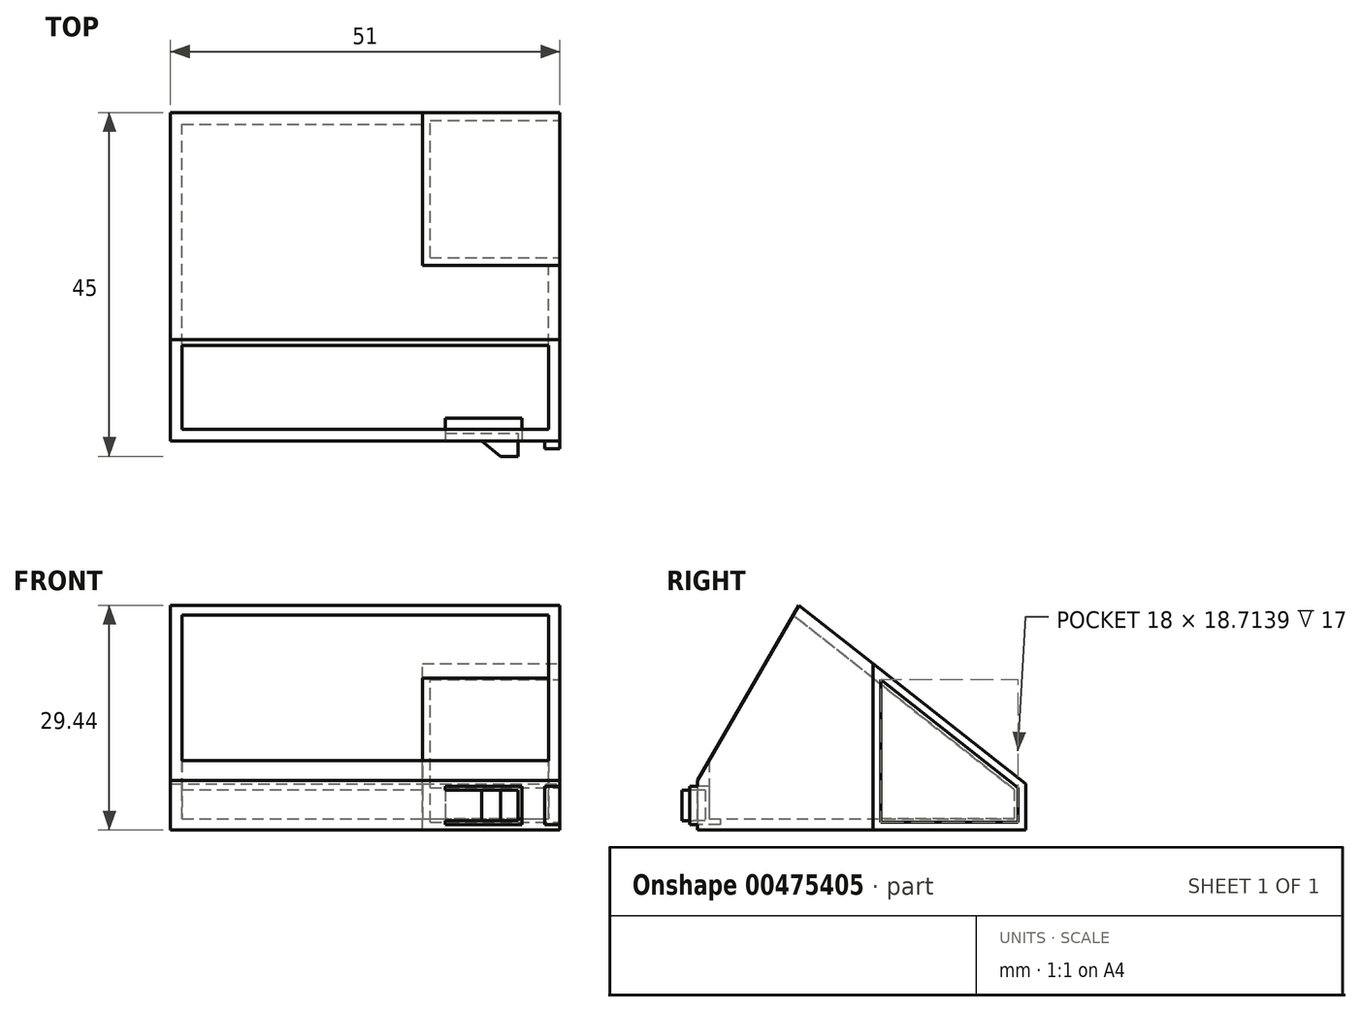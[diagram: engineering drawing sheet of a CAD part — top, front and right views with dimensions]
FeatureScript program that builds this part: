
annotation { "Feature Type Name" : "Feature", "Feature Type Description" : "" }
export const myFeature = defineFeature(function(context is Context, id is Id, definition is map)
    precondition{}
    {
        {
            var Q0;
            Q0=qCreatedBy(makeId("Right.planeOp"),FACE);
            var sketch = newSketch(context, id + "F0", { "sketchPlane" : qUnion([Q0])});
            skLineSegment(sketch, "E0.0", {"start": v(-18.73, 5.62) * mm, "end": v(-18.73, -0.85) * mm});
            skLineSegment(sketch, "E0.1", {"start": v(-5.47, 28.6) * mm, "end": v(-18.73, 5.62) * mm});
            skLineSegment(sketch, "E0.2", {"start": v(-18.73, -0.85) * mm, "end": v(24.27, -0.85) * mm});
            skLineSegment(sketch, "E0.3", {"start": v(24.27, -0.85) * mm, "end": v(24.27, 5.18) * mm});
            skLineSegment(sketch, "E0.4", {"start": v(24.27, 5.18) * mm, "end": v(-5.47, 28.6) * mm});
            skLineSegment(sketch, "E1", {"start": v(4.27, -0.85) * mm, "end": v(4.27, 20.93) * mm});
            skLineSegment(sketch, "E2", {"start": v(-18.73, 5.62) * mm, "end": v(4.27, 5.62) * mm});
            skSolve(sketch);
        }
        {
            var Q0;
            {var subQ0=sQuery(id+"F0.wireOp",EDGE,"E0.0");Q0=makeQuery(id+"F0.imprint","IMPRINT",FACE,{"disambiguationData":[TD([[makeQuery(id+"F0.imprint","IMPRINT",EDGE,{"derivedFrom":subQ0}),1.0]])]});}
            var Q1;
            {var subQ0=sQuery(id+"F0.wireOp",EDGE,"E0.1");Q1=makeQuery(id+"F0.imprint","IMPRINT",FACE,{"disambiguationData":[TD([[makeQuery(id+"F0.imprint","IMPRINT",EDGE,{"derivedFrom":subQ0}),1.0]])]});}
            var Q2;
            {var subQ5=sQuery(id+"F0.wireOp",EDGE,"E0.3");Q2=makeQuery(id+"F0.imprint","IMPRINT",FACE,{"disambiguationData":[TD([[makeQuery(id+"F0.imprint","IMPRINT",EDGE,{"derivedFrom":subQ5}),1.0]])]});}
            extrude(context, id + "F1", {"entities" : qUnion([Q0, Q1, Q2]), "oppositeDirection" : true, "depth" : 51 * mm});
        }
        {
            var Q0;
            Q0=makeQuery(id+"F1.opExtrude","SWEPT_FACE",FACE,{"disambiguationData":[OSD([sQuery(id+"F0.wireOp",EDGE,"E0.1")])]});
            shell(context, id + "F2", {"entities" : qUnion([Q0]), "thickness" : 1.5 * mm});
        }
        {
            var Q0;
            {var subQ5=sQuery(id+"F0.wireOp",EDGE,"E0.3");Q0=makeQuery(id+"F0.imprint","IMPRINT",FACE,{"disambiguationData":[TD([[makeQuery(id+"F0.imprint","IMPRINT",EDGE,{"derivedFrom":subQ5}),1.0]])]});}
            extrude(context, id + "F3", {"entities" : qUnion([Q0]), "operationType" : NewBodyOperationType.REMOVE, "oppositeDirection" : true, "depth" : 18 * mm});
        }
        {
            var Q0;
            {var subQ5=sQuery(id+"F0.wireOp",EDGE,"E0.3");Q0=makeQuery(id+"F0.imprint","IMPRINT",FACE,{"disambiguationData":[TD([[makeQuery(id+"F0.imprint","IMPRINT",EDGE,{"derivedFrom":subQ5}),1.0]])]});}
            extrude(context, id + "F4", {"entities" : qUnion([Q0]), "oppositeDirection" : true, "depth" : 18 * mm});
        }
        {
            var Q0;
            Q0=makeQuery(id+"F4.opExtrude","CAP_FACE",FACE,{"disambiguationData":[OSD([sQuery(id+"F0.wireOp",EDGE,"E0.2"),sQuery(id+"F0.wireOp",EDGE,"E0.3"),sQuery(id+"F0.wireOp",EDGE,"E0.4"),sQuery(id+"F0.wireOp",EDGE,"E1")])],"isStart":true});
            shell(context, id + "F5", {"entities" : qUnion([Q0]), "thickness" : 1 * mm});
        }
        {
            var Q0;
            Q0=makeQuery(id+"F1.opExtrude","SWEPT_FACE",FACE,{"disambiguationData":[OSD([sQuery(id+"F0.wireOp",EDGE,"E0.0")])]});
            var sketch = newSketch(context, id + "F6", { "sketchPlane" : qUnion([Q0])});
            skLineSegment(sketch, "E3.0.0", {"start": v(0, -0.85) * mm, "end": v(0, 5.62) * mm});
            skLineSegment(sketch, "E3.0.1", {"start": v(0, 5.62) * mm, "end": v(-51, 5.62) * mm});
            skLineSegment(sketch, "E3.0.2", {"start": v(-51, 5.62) * mm, "end": v(-51, -0.85) * mm});
            skLineSegment(sketch, "E3.0.3", {"start": v(-51, -0.85) * mm, "end": v(0, -0.85) * mm});
            skLineSegment(sketch, "E4.bottom", {"start": v(-5, 4.89) * mm, "end": v(-15, 4.89) * mm});
            skLineSegment(sketch, "E4.top", {"start": v(-5, -0.11) * mm, "end": v(-15, -0.11) * mm});
            skLineSegment(sketch, "E4.left", {"start": v(-5, 4.89) * mm, "end": v(-5, -0.11) * mm});
            skLineSegment(sketch, "E4.right", {"start": v(-15, 4.89) * mm, "end": v(-15, -0.11) * mm});
            skPoint(sketch, "E4.middle", {"position": v(-10, 2.39) * mm});
            skPoint(sketch, "E4.middle.positionSnap0", {"position": v(0, 2.39) * mm});
            skPoint(sketch, "E4.centerSnap0", {"position": v(0, 2.39) * mm});
            skLineSegment(sketch, "E5", {"start": v(0, 2.39) * mm, "end": v(-27.52, 2.39) * mm, "construction": true});
            skLineSegment(sketch, "E6.bottom", {"start": v(-15, 0.39) * mm, "end": v(-5.5, 0.39) * mm});
            skLineSegment(sketch, "E6.top", {"start": v(-15, 4.39) * mm, "end": v(-5.5, 4.39) * mm});
            skLineSegment(sketch, "E6.left", {"start": v(-15, 0.39) * mm, "end": v(-15, 4.39) * mm});
            skLineSegment(sketch, "E6.right", {"start": v(-5.5, 0.39) * mm, "end": v(-5.5, 4.39) * mm});
            skLineSegment(sketch, "E7.bottom", {"start": v(-2, 4.89) * mm, "end": v(0, 4.89) * mm});
            skLineSegment(sketch, "E7.top", {"start": v(-2, -0.11) * mm, "end": v(0, -0.11) * mm});
            skLineSegment(sketch, "E7.left", {"start": v(-2, 4.89) * mm, "end": v(-2, -0.11) * mm});
            skLineSegment(sketch, "E7.right", {"start": v(0, 4.89) * mm, "end": v(0, -0.11) * mm});
            skSolve(sketch);
        }
        {
            var Q0;
            Q0=makeQuery(id+"F6.imprint","IMPRINT",FACE,{"disambiguationData":[TD([[makeQuery(id+"F6.imprint","IMPRINT",EDGE,{"derivedFrom":sQuery(id+"F6.wireOp",EDGE,"E4.bottom")}),1.0]])]});
            var Q1;
            Q1=makeQuery(id+"F6.imprint","IMPRINT",FACE,{"disambiguationData":[TD([[makeQuery(id+"F6.imprint","IMPRINT",EDGE,{"derivedFrom":sQuery(id+"F6.wireOp",EDGE,"E6.bottom")}),1.0]])]});
            extrude(context, id + "F7", {"entities" : qUnion([Q0, Q1]), "operationType" : NewBodyOperationType.REMOVE, "oppositeDirection" : true, "depth" : 3 * mm});
        }
        {
            var Q0;
            Q0=makeQuery(id+"F6.imprint","IMPRINT",FACE,{"disambiguationData":[TD([[makeQuery(id+"F6.imprint","IMPRINT",EDGE,{"derivedFrom":sQuery(id+"F6.wireOp",EDGE,"E6.bottom")}),1.0]])]});
            extrude(context, id + "F8", {"entities" : qUnion([Q0]), "operationType" : NewBodyOperationType.ADD, "oppositeDirection" : true, "depth" : 1 * mm, "hasSecondDirection" : true, "secondDirectionOppositeDirection" : false, "secondDirectionDepth" : 2 * mm});
        }
        {
            var Q0;
            Q0=makeQuery(id+"F8.opExtrude","SWEPT_FACE",FACE,{"disambiguationData":[OSD([sQuery(id+"F6.wireOp",EDGE,"E6.top")])]});
            var sketch = newSketch(context, id + "F9", { "sketchPlane" : qUnion([Q0])});
            skLineSegment(sketch, "E8.0.0", {"start": v(-15, -20.73) * mm, "end": v(-5.5, -20.73) * mm});
            skLineSegment(sketch, "E8.0.1", {"start": v(-5.5, -20.73) * mm, "end": v(-5.5, -17.73) * mm});
            skLineSegment(sketch, "E8.0.2", {"start": v(-5.5, -17.73) * mm, "end": v(-15, -17.73) * mm});
            skLineSegment(sketch, "E8.0.3", {"start": v(-15, -17.73) * mm, "end": v(-15, -18.73) * mm});
            skLineSegment(sketch, "E8.0.4", {"start": v(-15, -18.73) * mm, "end": v(-15, -20.73) * mm});
            skLineSegment(sketch, "E9", {"start": v(-15, -18.73) * mm, "end": v(-10.25, -18.73) * mm});
            skPoint(sketch, "E9.endSnap0", {"position": v(-10.25, -20.73) * mm});
            skLineSegment(sketch, "E10", {"start": v(-10.25, -18.73) * mm, "end": v(-7.75, -20.73) * mm});
            skSolve(sketch);
        }
        {
            var Q0;
            {var subQ0=sQuery(id+"F9.wireOp",EDGE,"E8.0.4");Q0=makeQuery(id+"F9.imprint","IMPRINT",FACE,{"disambiguationData":[TD([[makeQuery(id+"F9.imprint","IMPRINT",EDGE,{"derivedFrom":subQ0}),1.0]])]});}
            extrude(context, id + "F10", {"entities" : qUnion([Q0]), "operationType" : NewBodyOperationType.REMOVE, "oppositeDirection" : true, "depth" : 25 * mm});
        }
        {
            var Q0;
            Q0=makeQuery(id+"F6.imprint","IMPRINT",FACE,{"disambiguationData":[TD([[makeQuery(id+"F6.imprint","IMPRINT",EDGE,{"derivedFrom":sQuery(id+"F6.wireOp",EDGE,"E7.bottom")}),-1.0]])]});
            extrude(context, id + "F11", {"entities" : qUnion([Q0]), "operationType" : NewBodyOperationType.ADD, "depth" : 1 * mm});
        }
    });
